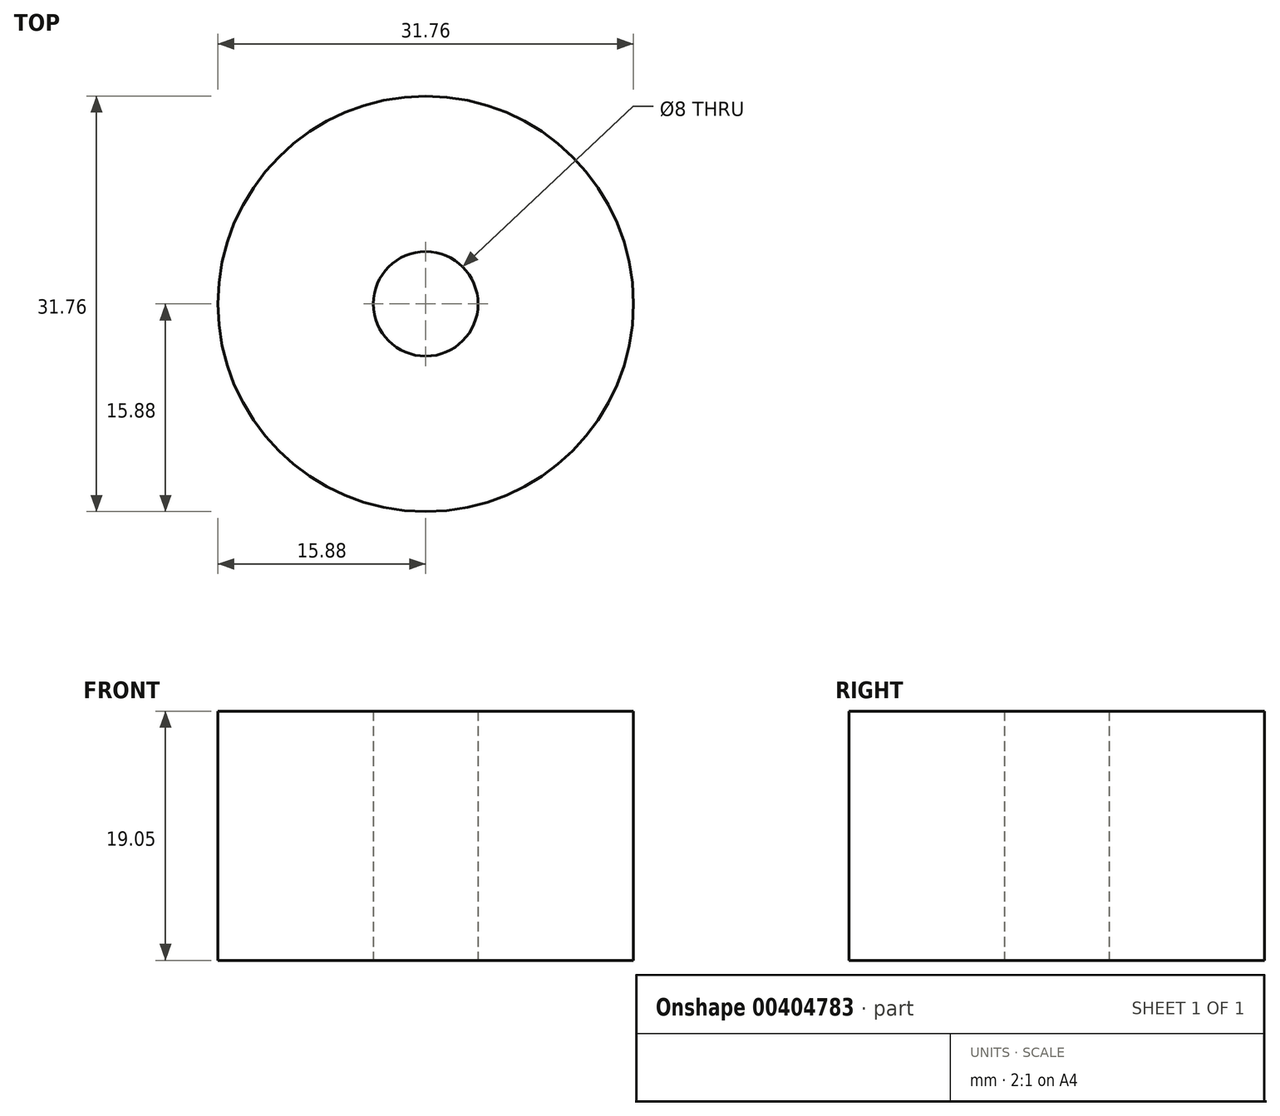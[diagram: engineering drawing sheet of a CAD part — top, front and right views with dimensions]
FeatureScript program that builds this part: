
annotation { "Feature Type Name" : "Feature", "Feature Type Description" : "" }
export const myFeature = defineFeature(function(context is Context, id is Id, definition is map)
    precondition{}
    {
        {
            var Q0;
            Q0=qCreatedBy(makeId("Top.planeOp"),FACE);
            var sketch = newSketch(context, id + "F0", { "sketchPlane" : qUnion([Q0])});
            skCircle(sketch, "E0", {"center": v(0, 0) * mm, "radius": 15.88 * mm});
            skCircle(sketch, "E1", {"center": v(0, 0) * mm, "radius": 4 * mm});
            skSolve(sketch);
        }
        {
            var Q0;
            Q0=makeQuery(id+"F0.imprint","IMPRINT",FACE,{"disambiguationData":[TD([[makeQuery(id+"F0.imprint","IMPRINT",EDGE,{"derivedFrom":sQuery(id+"F0.wireOp",EDGE,"E0")}),1.0]])]});
            extrude(context, id + "F1", {"entities" : qUnion([Q0]), "depth" : 19.05 * mm});
        }
    });
